# Revit family: 6DMLH-NRG
name_source: partatom
category: Mechanical Equipment
units: mm (PartAtom-declared; Revit-internal decimal feet)

## family parameters
Always vertical = Yes
Cut with Voids When Loaded = No
OmniClass Number = 23.40.40.11.17
OmniClass Title = Refrigerated Cases
Part Type = Normal
Room Calculation Point = No
Round Connector Dimension = Use Radius
Shared = No
Work Plane-Based = Yes

## types (4) — shared parameters
24" Shelf = Yes
BOTTOM ELECTRICAL = Yes
BOTTOM REFRIGERATION PIPING = Yes
Certifications = NSF 7, UL471, CSA
DATE = 04/29/2016
DESIGNERS NAME = SHIDDRAMESH
DRAIN PIPING = Yes
Default Elevation = 48"
Description = High Multi-Deck Merchandiser with Synerg-E™
EQUIPMENT DESCRIPTION = High Multi-Deck Merchandiser with Synerg-E™
EQUIPMENT MARK = 6DMLH-NRG
GLASS = Glass
Height = 88 5/8"
Item Description = High Multi-Deck Merchandiser with Synerg-E™
Legend Number = 6DMLH-NRG
Length of Cases = 144"
Manufacturer = HILL PHOENIX
Model = 6DMLH-NRG
PAINTED METAL UPPER SHELF = PAINTED SHELVES
REFRIGERATION PIPING = COPPER PIPE
SQUARE END LH = Yes
SQUARE END RH = Yes
STAINLESS STEEL = GALVANIZED STEEL
TOP ELECTRICAL = Yes
TOP REFRIGERATION PIPING = Yes
URL = http://www.hillphoenix.com
Width = 42 3/4"

## per-type parameters (varying)
| type | DRAIN LINE | FULL VIEW LH END | FULL VIEW RH END | KP LH | KP RH | LF STD END | Length | REDUCED RH END | REDUCED VIEW LH END | RT STD END | SOLID EXT LH END | SOLID EXT RH END | SOLID STD LH END | SOLID STD RH END | SUPER VIEW LH END | SUPER VIEW RH END |
| 12' | 72" | No | No | Yes | Yes | No | 144" | No | No | No | No | No | No | No | No | No |
| 8' | 48" | Yes | Yes | No | No | No | 96" | Yes | Yes | No | Yes | Yes | Yes | Yes | Yes | Yes |
| 6' | 36" | Yes | Yes | No | No | Yes | 72" | Yes | Yes | Yes | Yes | Yes | Yes | Yes | Yes | Yes |
| 4' | 24" | Yes | Yes | No | No | Yes | 48" | Yes | Yes | Yes | Yes | Yes | Yes | Yes | Yes | Yes |

## geometry (parser evidence)
native form markers: Blend x4, Sweep x12
no freeform markers — native parametric forms only
